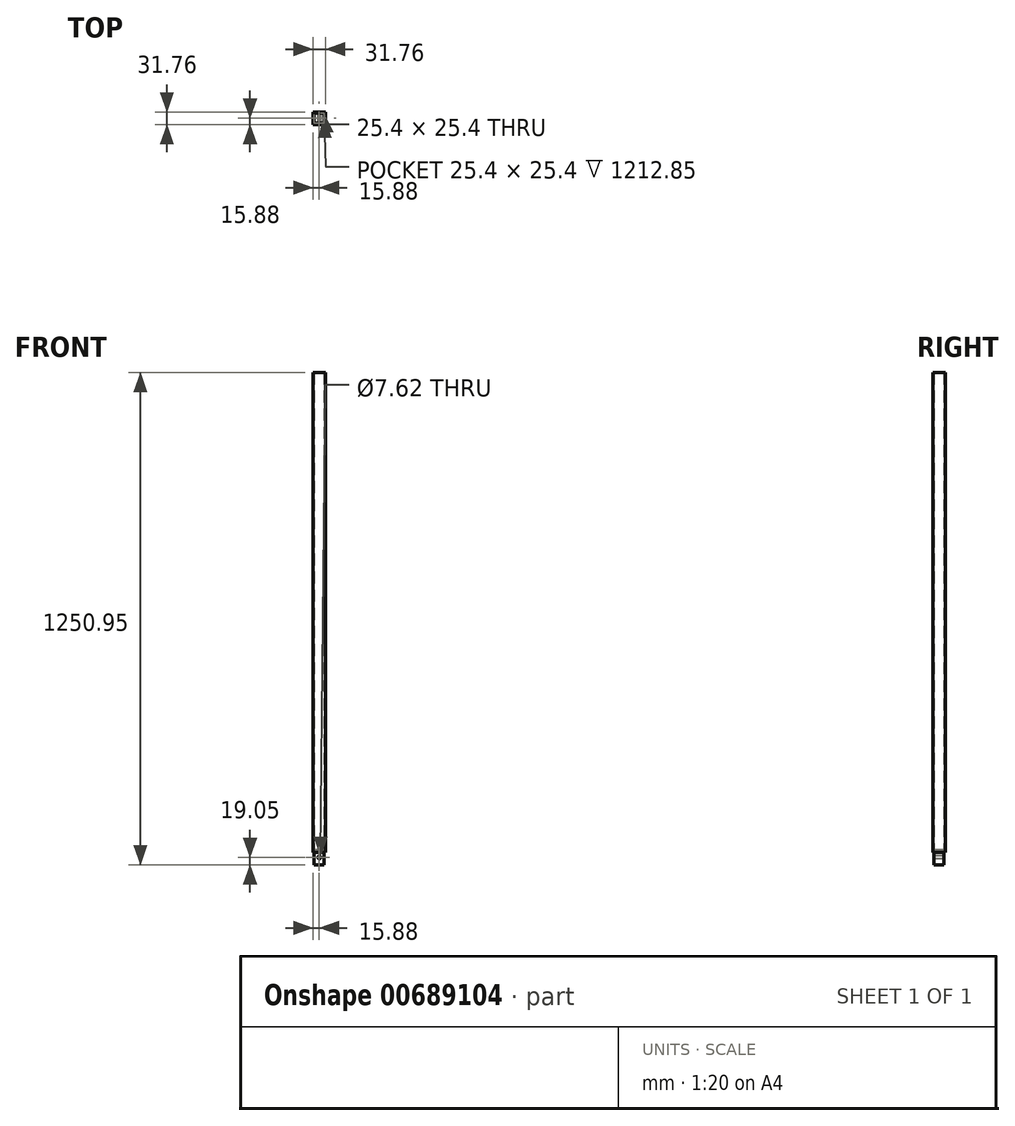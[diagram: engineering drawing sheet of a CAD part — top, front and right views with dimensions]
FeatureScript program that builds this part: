
annotation { "Feature Type Name" : "Feature", "Feature Type Description" : "" }
export const myFeature = defineFeature(function(context is Context, id is Id, definition is map)
    precondition{}
    {
        {
            var Q0;
            Q0=qCreatedBy(makeId("Top.planeOp"),FACE);
            var sketch = newSketch(context, id + "F0", { "sketchPlane" : qUnion([Q0])});
            skLineSegment(sketch, "E0.bottom", {"start": v(-15.88, 15.88) * mm, "end": v(15.88, 15.88) * mm});
            skLineSegment(sketch, "E0.top", {"start": v(-15.88, -15.87) * mm, "end": v(15.88, -15.87) * mm});
            skLineSegment(sketch, "E0.left", {"start": v(-15.88, 15.88) * mm, "end": v(-15.88, -15.87) * mm});
            skLineSegment(sketch, "E0.right", {"start": v(15.88, 15.88) * mm, "end": v(15.88, -15.87) * mm});
            skLineSegment(sketch, "E1.0", {"start": v(-12.7, 12.7) * mm, "end": v(-12.7, -12.7) * mm});
            skLineSegment(sketch, "E1.1", {"start": v(-12.7, 12.7) * mm, "end": v(12.7, 12.7) * mm});
            skLineSegment(sketch, "E1.2", {"start": v(12.7, 12.7) * mm, "end": v(12.7, -12.7) * mm});
            skLineSegment(sketch, "E1.3", {"start": v(-12.7, -12.7) * mm, "end": v(12.7, -12.7) * mm});
            skSolve(sketch);
        }
        {
            var Q0;
            Q0=makeQuery(id+"F0.imprint","IMPRINT",FACE,{"disambiguationData":[TD([[makeQuery(id+"F0.imprint","IMPRINT",EDGE,{"derivedFrom":sQuery(id+"F0.wireOp",EDGE,"E0.bottom")}),-1.0]])]});
            extrude(context, id + "F1", {"entities" : qUnion([Q0]), "depth" : 1219.2 * mm, "offsetDistance" : 25.4 * mm});
        }
        {
            var Q0;
            Q0=makeQuery(id+"F1.opExtrude","CAP_FACE",FACE,{"disambiguationData":[OSD([sQuery(id+"F0.wireOp",EDGE,"E0.bottom"),sQuery(id+"F0.wireOp",EDGE,"E0.top"),sQuery(id+"F0.wireOp",EDGE,"E0.left"),sQuery(id+"F0.wireOp",EDGE,"E0.right"),sQuery(id+"F0.wireOp",EDGE,"E1.0"),sQuery(id+"F0.wireOp",EDGE,"E1.1"),sQuery(id+"F0.wireOp",EDGE,"E1.2"),sQuery(id+"F0.wireOp",EDGE,"E1.3")])],"isStart":true});
            var sketch = newSketch(context, id + "F2", { "sketchPlane" : qUnion([Q0])});
            skLineSegment(sketch, "E2.bottom", {"start": v(-12.7, -12.7) * mm, "end": v(12.7, -12.7) * mm});
            skLineSegment(sketch, "E2.top", {"start": v(-12.7, 12.7) * mm, "end": v(12.7, 12.7) * mm});
            skLineSegment(sketch, "E2.left", {"start": v(-12.7, -12.7) * mm, "end": v(-12.7, 12.7) * mm});
            skLineSegment(sketch, "E2.right", {"start": v(12.7, -12.7) * mm, "end": v(12.7, 12.7) * mm});
            skSolve(sketch);
        }
        {
            var Q0;
            Q0=makeQuery(id+"F2.imprint","IMPRINT",FACE,{"disambiguationData":[TD([[makeQuery(id+"F2.imprint","IMPRINT",EDGE,{"derivedFrom":sQuery(id+"F2.wireOp",EDGE,"E2.bottom")}),1.0]])]});
            extrude(context, id + "F3", {"entities" : qUnion([Q0]), "depth" : 31.75 * mm, "offsetDistance" : 25.4 * mm});
        }
        {
            var Q0;
            Q0=makeQuery(id+"F3.opExtrude","SWEPT_FACE",FACE,{"disambiguationData":[OSD([sQuery(id+"F2.wireOp",EDGE,"E2.top")])]});
            var sketch = newSketch(context, id + "F4", { "sketchPlane" : qUnion([Q0])});
            skCircle(sketch, "E3", {"center": v(0, -12.7) * mm, "radius": 3.81 * mm});
            skSolve(sketch);
        }
        {
            var Q0;
            Q0=makeQuery(id+"F4.imprint","IMPRINT",FACE,{"disambiguationData":[TD([[makeQuery(id+"F4.imprint","IMPRINT",EDGE,{"derivedFrom":sQuery(id+"F4.wireOp",EDGE,"E3")}),1.0]])]});
            extrude(context, id + "F5", {"entities" : qUnion([Q0]), "operationType" : NewBodyOperationType.REMOVE, "endBound" : BoundingType.THROUGH_ALL, "oppositeDirection" : true, "depth" : 25.4 * mm, "offsetDistance" : 25.4 * mm});
        }
        {
            var Q0;
            Q0=makeQuery(id+"F3.opExtrude","SWEPT_BODY",BODY,{"disambiguationData":[OSD([sQuery(id+"F2.wireOp",EDGE,"E2.bottom"),sQuery(id+"F2.wireOp",EDGE,"E2.top"),sQuery(id+"F2.wireOp",EDGE,"E2.left"),sQuery(id+"F2.wireOp",EDGE,"E2.right")])]});
            deleteBodies(context, id + "F6", {"entities" : qUnion([Q0])});
        }
        {
            var Q0;
            Q0=makeQuery(id+"F1.opExtrude","SWEPT_FACE",FACE,{"disambiguationData":[OSD([sQuery(id+"F0.wireOp",EDGE,"E1.0")])]});
            var sketch = newSketch(context, id + "F7", { "sketchPlane" : qUnion([Q0])});
            skLineSegment(sketch, "E4.bottom", {"start": v(12.7, 6.35) * mm, "end": v(-12.7, 6.35) * mm});
            skLineSegment(sketch, "E4.top", {"start": v(12.7, -31.75) * mm, "end": v(-12.7, -31.75) * mm});
            skLineSegment(sketch, "E4.left", {"start": v(12.7, 6.35) * mm, "end": v(12.7, -31.75) * mm});
            skLineSegment(sketch, "E4.right", {"start": v(-12.7, 6.35) * mm, "end": v(-12.7, -31.75) * mm});
            skSolve(sketch);
        }
        {
            var Q0;
            {var subQ0=sQuery(id+"F7.wireOp",EDGE,"E4.bottom");Q0=makeQuery(id+"F7.imprint","IMPRINT",FACE,{"disambiguationData":[TD([[makeQuery(id+"F7.imprint","IMPRINT",EDGE,{"derivedFrom":subQ0}),1.0]])]});}
            var Q1;
            {var subQ0=sQuery(id+"F7.wireOp",EDGE,"E4.top");Q1=makeQuery(id+"F7.imprint","IMPRINT",FACE,{"disambiguationData":[TD([[makeQuery(id+"F7.imprint","IMPRINT",EDGE,{"derivedFrom":subQ0}),-1.0]])]});}
            extrude(context, id + "F8", {"entities" : qUnion([Q0, Q1]), "operationType" : NewBodyOperationType.ADD, "depth" : 25.4 * mm, "offsetDistance" : 25.4 * mm});
        }
        {
            var Q0;
            Q0=makeQuery(id+"F8.opExtrude","SWEPT_FACE",FACE,{"disambiguationData":[OSD([sQuery(id+"F7.wireOp",EDGE,"E4.right")])]});
            var sketch = newSketch(context, id + "F9", { "sketchPlane" : qUnion([Q0])});
            skCircle(sketch, "E5", {"center": v(0, -12.7) * mm, "radius": 3.81 * mm});
            skSolve(sketch);
        }
        {
            var Q0;
            Q0=makeQuery(id+"F9.imprint","IMPRINT",FACE,{"disambiguationData":[TD([[makeQuery(id+"F9.imprint","IMPRINT",EDGE,{"derivedFrom":sQuery(id+"F9.wireOp",EDGE,"E5")}),1.0]])]});
            extrude(context, id + "F10", {"entities" : qUnion([Q0]), "operationType" : NewBodyOperationType.REMOVE, "endBound" : BoundingType.THROUGH_ALL, "oppositeDirection" : true, "depth" : 25.4 * mm, "offsetDistance" : 25.4 * mm});
        }
    });
